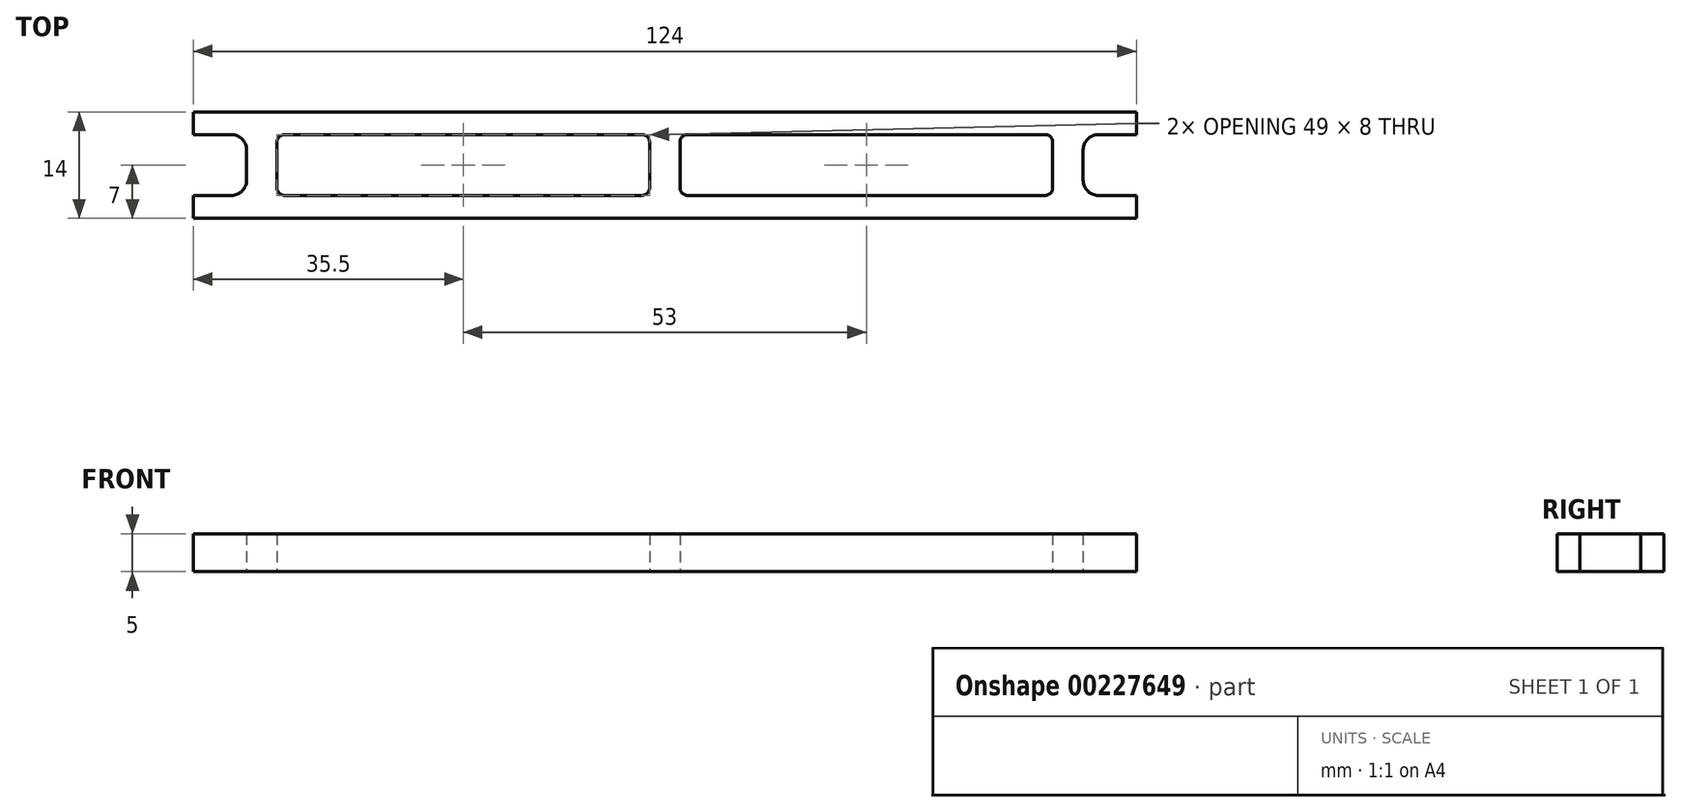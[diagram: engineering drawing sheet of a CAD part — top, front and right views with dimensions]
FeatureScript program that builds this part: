
annotation { "Feature Type Name" : "Feature", "Feature Type Description" : "" }
export const myFeature = defineFeature(function(context is Context, id is Id, definition is map)
    precondition{}
    {
        {
            var Q0;
            Q0=qCreatedBy(makeId("Top.planeOp"),FACE);
            var sketch = newSketch(context, id + "F0", { "sketchPlane" : qUnion([Q0])});
            skLineSegment(sketch, "E0", {"start": v(0, 0) * mm, "end": v(62, 0) * mm});
            skLineSegment(sketch, "E1", {"start": v(62, 0) * mm, "end": v(62, 3) * mm});
            skLineSegment(sketch, "E2", {"start": v(62, 3) * mm, "end": v(55, 3) * mm});
            skLineSegment(sketch, "E3", {"start": v(55, 3) * mm, "end": v(55, 7) * mm});
            skLineSegment(sketch, "E4", {"start": v(55, 7) * mm, "end": v(51, 7) * mm});
            skLineSegment(sketch, "E5", {"start": v(51, 7) * mm, "end": v(51, 3) * mm});
            skLineSegment(sketch, "E6", {"start": v(51, 3) * mm, "end": v(2, 3) * mm});
            skLineSegment(sketch, "E7", {"start": v(2, 3) * mm, "end": v(2, 7) * mm});
            skLineSegment(sketch, "E8", {"start": v(2, 7) * mm, "end": v(0, 7) * mm});
            skLineSegment(sketch, "E9", {"start": v(0, 7) * mm, "end": v(0, 3) * mm});
            skLineSegment(sketch, "E10", {"start": v(0, 3) * mm, "end": v(0, 0) * mm});
            skSolve(sketch);
        }
        {
            var Q0;
            Q0=makeQuery(id+"F0.imprint","IMPRINT",FACE,{"disambiguationData":[TD([[makeQuery(id+"F0.imprint","IMPRINT",EDGE,{"derivedFrom":sQuery(id+"F0.wireOp",EDGE,"E0")}),1.0]])]});
            extrude(context, id + "F1", {"entities" : qUnion([Q0]), "depth" : 5 * mm});
        }
        {
            var Q0;
            Q0=makeQuery(id+"F1.opExtrude","SWEPT_EDGE",EDGE,{"disambiguationData":[OSD([sQuery(id+"F0.wireOp",EDGE,"E2"),sQuery(id+"F0.wireOp",EDGE,"E3")])]});
            fillet(context, id + "F2", {"entities" : qUnion([Q0]), "radius" : 2 * mm, "tangentPropagation" : true, "allowEdgeOverflow" : false});
        }
        {
            var Q0;
            Q0=makeQuery(id+"F1.opExtrude","SWEPT_EDGE",EDGE,{"disambiguationData":[OSD([sQuery(id+"F0.wireOp",EDGE,"E5"),sQuery(id+"F0.wireOp",EDGE,"E6")])]});
            var Q1;
            Q1=makeQuery(id+"F1.opExtrude","SWEPT_EDGE",EDGE,{"disambiguationData":[OSD([sQuery(id+"F0.wireOp",EDGE,"E6"),sQuery(id+"F0.wireOp",EDGE,"E7")])]});
            fillet(context, id + "F3", {"entities" : qUnion([Q0, Q1]), "radius" : 1 * mm, "tangentPropagation" : true, "allowEdgeOverflow" : false});
        }
        {
            var Q0;
            Q0=makeQuery(id+"F1.opExtrude","SWEPT_BODY",BODY,{"disambiguationData":[OSD([sQuery(id+"F0.wireOp",EDGE,"E0"),sQuery(id+"F0.wireOp",EDGE,"E1"),sQuery(id+"F0.wireOp",EDGE,"E2"),sQuery(id+"F0.wireOp",EDGE,"E3"),sQuery(id+"F0.wireOp",EDGE,"E4"),sQuery(id+"F0.wireOp",EDGE,"E5"),sQuery(id+"F0.wireOp",EDGE,"E6"),sQuery(id+"F0.wireOp",EDGE,"E7"),sQuery(id+"F0.wireOp",EDGE,"E8"),sQuery(id+"F0.wireOp",EDGE,"E9"),sQuery(id+"F0.wireOp",EDGE,"E10")])]});
            var Q1;
            Q1=makeQuery(id+"F1.opExtrude","SWEPT_FACE",FACE,{"disambiguationData":[OSD([sQuery(id+"F0.wireOp",EDGE,"E9"),sQuery(id+"F0.wireOp",EDGE,"E10")])]});
            mirror(context, id + "F4", {"operationType" : NewBodyOperationType.ADD, "entities" : qUnion([Q0]), "mirrorPlane" : qUnion([Q1])});
        }
        {
            var Q0;
            Q0=makeQuery(id+"F1.opExtrude","SWEPT_BODY",BODY,{"disambiguationData":[OSD([sQuery(id+"F0.wireOp",EDGE,"E0"),sQuery(id+"F0.wireOp",EDGE,"E1"),sQuery(id+"F0.wireOp",EDGE,"E2"),sQuery(id+"F0.wireOp",EDGE,"E3"),sQuery(id+"F0.wireOp",EDGE,"E4"),sQuery(id+"F0.wireOp",EDGE,"E5"),sQuery(id+"F0.wireOp",EDGE,"E6"),sQuery(id+"F0.wireOp",EDGE,"E7"),sQuery(id+"F0.wireOp",EDGE,"E8"),sQuery(id+"F0.wireOp",EDGE,"E9"),sQuery(id+"F0.wireOp",EDGE,"E10")])]});
            var Q1;
            {var subQ0=makeQuery(id+"F1.opExtrude","SWEPT_FACE",FACE,{"disambiguationData":[OSD([sQuery(id+"F0.wireOp",EDGE,"E8")])]});Q1=makeQuery(id+"F4.boolean.opBoolean","MERGE",FACE,{"derivedFrom":[subQ0,makeQuery(id+"F4.opPattern","COPY",FACE,{"derivedFrom":subQ0,"instanceName":"1"})]});}
            mirror(context, id + "F5", {"operationType" : NewBodyOperationType.ADD, "entities" : qUnion([Q0]), "mirrorPlane" : qUnion([Q1])});
        }
    });
